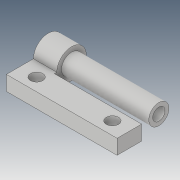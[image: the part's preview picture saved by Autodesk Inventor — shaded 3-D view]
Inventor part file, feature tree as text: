
AUTODESK INVENTOR PART (.ipt)
format: ipt  version: 2019 (Build 230136000, 136)  size: 182,784 bytes
history: native  units: mm
features: extrude x7, sketch x6, plane x5, other x3, move_body x2, fillet x1, direct_edit x1, projected_geometry x1
ambient origin geometry x8: Origin, YZ Plane, XZ Plane, XY Plane, X Axis, Y Axis, Z Axis, Center Point
bodies: Solid1 (feature_tree)
feature tree (26):
  extrude  "Extrusion1"  Depth=45.0mm
  sketch  "Sketch4"  dims[d5=5.0mm d6=5.0mm d7=11.0mm]
  extrude  "Extrusion4"  Depth=5.0mm
  fillet  "Fillet1"  Radius=11.0mm
  extrude  "Extrusion5"  Depth=23.0mm
  plane  "Work Plane1"
  extrude  "Extrusion6"  Depth=12.0mm
  plane  "Work Plane8"
  plane  "Work Plane10"
  sketch  "Sketch11"  dims[d21=0.0mm d24=3.0mm d25=0.0mm]
  plane  "Work Plane11"
  plane  "Work Plane12"
  extrude  "Extrusion10"  Depth=3.0mm TaperAngle=0.0deg
  extrude  "Extrusion11"  Depth=10.0mm
  direct_edit  "Direct Edit1"
  extrude  "Extrusion13"  Depth=10.0mm TaperAngle=0.0deg
  sketch  "Sketch1"  dims[d0=6.0mm d1=0.0mm d4=45.0mm]
  sketch  "Sketch5"  dims[d8=11.0mm d9=23.0mm]
  sketch  "Sketch6"  dims[d10=10.0mm d20=12.0mm]
  projected_geometry  "Projected Loop4"
  sketch  "Sketch13"  dims[d26=12.0mm d27=5.0mm d28=3.0mm d29=0.0mm d33=5.0mm d34=5.0mm d35=17.8mm d36=7.0mm d37=17.8mm d38=7.1mm d39=30.8mm d40=7.1mm d41=3.0mm d42=0.0mm d52=0.0mm d53=0.0mm d54=0.0mm d55=10.0mm d56=0.0mm d57=10.0mm d58=0.0mm d59=0.0mm d60=0.0mm d61=-1.5mm d62=0.0mm d63=0.0mm d64=-17.25mm d68=1.6mm d69=10.0mm d70=0.0mm]
  move_body  "Move1"
  move_body  "Move2"
  parser-record x1  (decoder bookkeeping rows leaked as tree rows — omitted from the tree; the rows remain in map.json)
  other  "Cerniera Assemb.iam"
  other  "Cerniera 1:2"
note: 1 file-system path scrubbed to <path> (originals preserved in map.json)
